# Revit family: HVAC_Heaters_Enertech_CTC-EcoZenith-i360H
name_source: partatom
category: Specialty Equipment
revit_build: Autodesk Revit 2017 (Build: 20190508_0315(x64)
units: mm (PartAtom-declared; Revit-internal decimal feet)

## family parameters
Always vertical = Yes
Cut with Voids When Loaded = No
OmniClass Number = 23.75.00.00
OmniClass Title = Climate Control (HVAC)
Part Type = Normal
Room Calculation Point = No
Round Connector Dimension = Use Diameter
Shared = No
Work Plane-Based = No

## types (1)
- CTC EcoZenith i360 High - 400V3N
    AssetType = Fixed
    BIMObjectName = HVAC_Heaters_Enertech_CTC-EcoZenith-i360H
    Brand = CTC
    Category = Indoor Module
    Color = white
    ConvergoRefNr = 0091-1710-0015-SE
    Cost = 0 $
    Description = Ultra-efficient indoor module available in two heights with built-in heat pump control and hot water preparation. The CTC EcoZenith i360  has internet connection as standard, so you can easily control your product remotely. It is also prepared for connection to Alexa and Google Home, etc.
    DurationUnit = Year
    EANNumber = 7333077094478
    ElectricalDeviceNominalPower = 11900 W
    EnergyClassHeatingWithControl = A+++ / A+++ (with heatpump)
    EnergyClass_HotWater_TapProfile = A+++ / XL
    GroupFuse = 20 A
    HasProtectiveEarth = Yes
    HotTapWaterPerformance = 210 - 304 liters
    IP_Code = IP X1
    IfcExportAs = IfcElectricalDeviceCommon
    IfcExportType = HEATER
    Manufacturer = Enertech AB
    ManufacturerCountry = Sweden
    ManufacturerName = Enertech AB
    ManufacturerURL = https://ctc.se
    Material = Steel/copper
    MaxOperatingPressureHotWater = 10 bar
    MaxOperatingPressureThermalStore = 3 bar
    MinimumCeilingHeight = 1928 mm
    Model = CTC EcoZenith i360 High
    ModelNumber = 589401001
    NBSDescription = Air to water heat pumps
    NBSReference = 90-40-40/320
    Name = CTC-EcoZenith-i360H
    NominalCurrent = 0 A
    NominalDepth = 673 mm  [stored 2.20801 ft]
    NominalFrequencyRange = 50 Hz
    NominalHeight = 1825 mm  [stored 5.98753 ft]
    NominalVoltage = 400 V
    NominalWidth = 596 mm  [stored 1.95538 ft]
    NumberOfPoles = 3
    OutputRangeIimmersionHeater = 0.5 - 11.9 kW
    PhaseAngle = 0.00°
    PowerFactor = 0 W
    ProductInformation = Ultra-efficient indoor module available in two heights with built-in heat pump control and hot water preparation. The CTC EcoZenith i360  has internet connection as standard, so you can easily control your product remotely. It is also prepared for connection to Alexa and Google Home, etc.
    PumpMainMaterial = Stainless Steel
    PumpSecondaryMaterial = Plastic, Opaque Black
    PumpTertiaryMaterial = Copper
    RatedCurrent = 19 A
    RatedHeatOutputModerate = 12 kW
    RatedVoltage = 1200 V
    Shape = Rectangular
    Size = 673x596x1907 mm
    Touchscreen = yes
    UNSPSCCode = 40102003
    URL = https://ctc-heating.com
    Uniclass2 = Pr_40_70_65
    Uniclass2015Description = Preparation catering equipment
    Uniclass2015Reference = Pr_40_70_65
    UsageCurrent = 0 A
    Version = 1
    VersionDate = 09/12/2020
    WarrantyDurationUnit = Year
    WaterVolumeHeathingSystem = 225 liters
    WaterVolumeWaterSuply = 225 liters
    Weight = 156 kg

note: [stored X ft] marks values corroborated as IEEE doubles in the binary element streams (Revit-internal decimal feet)

## geometry (parser evidence)
native form markers: Sweep x5
no freeform markers — native parametric forms only
